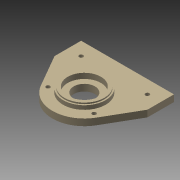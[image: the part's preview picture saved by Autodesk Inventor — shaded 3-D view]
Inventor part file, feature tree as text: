
AUTODESK INVENTOR PART (.ipt)
format: ipt  version: 2015 (Build 190159000, 159)  size: 154,112 bytes
history: native  units: mm
features: extrude x6, sketch x6
ambient origin geometry x8: Origin, YZ Plane, XZ Plane, XY Plane, X Axis, Y Axis, Z Axis, Center Point
bodies: 实体1 (feature_tree)
feature tree (12):
  extrude  "拉伸1"  Depth=15.910891mm
  extrude  "拉伸2"  Depth=20.0mm
  extrude  "拉伸3"  Depth=5.0mm TaperAngle=0.0deg
  extrude  "拉伸4"  Depth=25.0mm
  extrude  "拉伸5"  Depth=4.0mm
  extrude  "拉伸6"  Depth=1.0mm TaperAngle=0.0deg
  sketch  "草图1"  dims[d0=48.0mm d1=15.910891mm]
  sketch  "草图2"  dims[d2=12.5mm d3=20.0mm]
  sketch  "草图3"  dims[d4=150.0deg d5=5.0mm d6=0.0mm]
  sketch  "草图4"  dims[d7=32.0mm d8=25.0mm]
  sketch  "草图5"  dims[d9=4.0mm d10=0.0mm d11=32.0mm]
  sketch  "草图6"  dims[d12=30.0mm d13=1.0mm d14=0.0mm d15=16.0mm d16=1.0mm d17=0.0mm d18=3.0mm d19=3.0mm d20=3.0mm d21=3.0mm d22=10.0mm d23=10.0mm d24=10.0mm d25=10.0mm d26=10.0mm d27=20.0mm d28=10.0mm d29=1.0mm d30=0.0mm d31=5.0mm d32=5.0mm d33=5.0mm d34=5.0mm d35=2.5mm d36=0.0mm]
